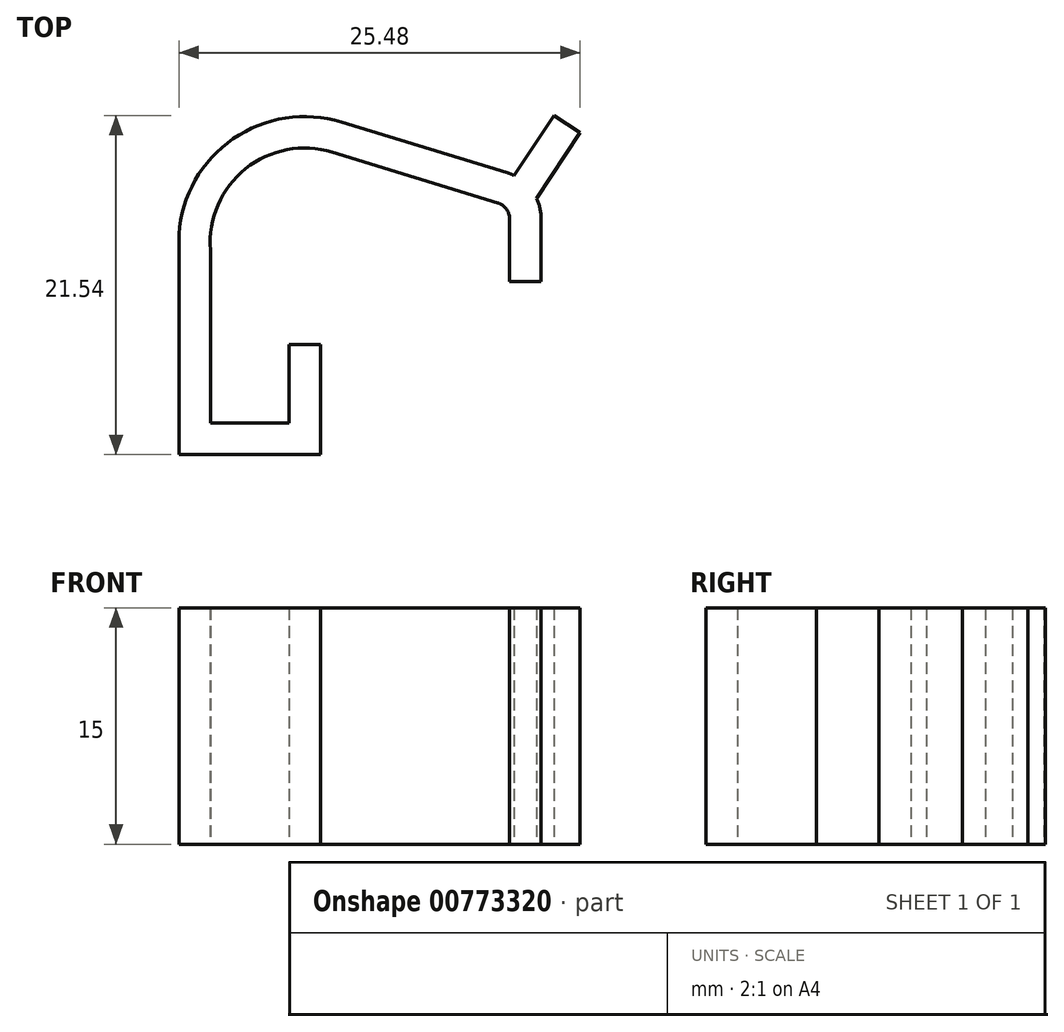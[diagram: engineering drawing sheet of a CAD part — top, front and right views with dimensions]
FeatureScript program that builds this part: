
annotation { "Feature Type Name" : "Feature", "Feature Type Description" : "" }
export const myFeature = defineFeature(function(context is Context, id is Id, definition is map)
    precondition{}
    {
        {
            var Q0;
            Q0=qCreatedBy(makeId("Top.planeOp"),FACE);
            var sketch = newSketch(context, id + "F0", { "sketchPlane" : qUnion([Q0])});
            skLineSegment(sketch, "E0", {"start": v(2, 32) * mm, "end": v(7, 32) * mm});
            skLineSegment(sketch, "E1", {"start": v(7, 32) * mm, "end": v(7, 37) * mm});
            skLineSegment(sketch, "E2", {"start": v(7, 37) * mm, "end": v(9, 37) * mm});
            skLineSegment(sketch, "E3", {"start": v(9, 37) * mm, "end": v(9, 30) * mm});
            skLineSegment(sketch, "E4", {"start": v(9, 30) * mm, "end": v(0, 30) * mm});
            skLineSegment(sketch, "E5", {"start": v(0, 30) * mm, "end": v(0, 44) * mm});
            skLineSegment(sketch, "E6", {"start": v(2, 32) * mm, "end": v(2, 43) * mm});
            skArc(sketch, "E7", {"start": v(9.74, 49.2) * mm, "mid": v(4.23, 48.15) * mm, "end": v(2, 43) * mm});
            skArc(sketch, "E8", {"start": v(10.32, 51.11) * mm, "mid": v(3.44, 50.05) * mm, "end": v(0, 44) * mm});
            skLineSegment(sketch, "E9", {"start": v(9.74, 49.2) * mm, "end": v(20.26, 45.98) * mm});
            skArc(sketch, "E10", {"start": v(20.26, 45.98) * mm, "mid": v(20.8, 45.6) * mm, "end": v(21, 44.98) * mm});
            skLineSegment(sketch, "E11", {"start": v(21, 44.98) * mm, "end": v(21, 40.98) * mm});
            skLineSegment(sketch, "E12", {"start": v(21, 40.98) * mm, "end": v(23, 40.98) * mm});
            skLineSegment(sketch, "E13", {"start": v(23, 44.98) * mm, "end": v(23, 40.98) * mm});
            skLineSegment(sketch, "E14", {"start": v(21.28, 47.72) * mm, "end": v(23.81, 51.54) * mm});
            skLineSegment(sketch, "E15", {"start": v(23.81, 51.54) * mm, "end": v(25.48, 50.43) * mm});
            skLineSegment(sketch, "E16", {"start": v(25.48, 50.43) * mm, "end": v(22.71, 46.27) * mm});
            skLineSegment(sketch, "E17", {"start": v(10.32, 51.11) * mm, "end": v(20.84, 47.9) * mm});
            skLineSegment(sketch, "E18", {"start": v(10.32, 51.11) * mm, "end": v(9.74, 49.2) * mm});
            skLineSegment(sketch, "E19", {"start": v(20.84, 47.9) * mm, "end": v(20.26, 45.98) * mm});
            skLineSegment(sketch, "E20", {"start": v(21, 44.98) * mm, "end": v(23, 44.98) * mm});
            skArc(sketch, "E21", {"start": v(20.84, 47.9) * mm, "mid": v(22.4, 46.8) * mm, "end": v(23, 44.98) * mm});
            skSolve(sketch);
        }
        {
            var Q0;
            Q0 = qSketchRegion(id + "F0", true);
            var Q1;
            Q1 = qSketchRegion(id + "F2", true);
            extrude(context, id + "F1", {"entities" : qUnion([Q0, Q1]), "depth" : 15 * mm, "offsetDistance" : 25 * mm});
        }
        {
            var Q0;
            Q0=qCreatedBy(makeId("Top.planeOp"),FACE);
            var sketch = newSketch(context, id + "F2", { "sketchPlane" : qUnion([Q0])});
            skLineSegment(sketch, "E22.0.1.0", {"start": v(-38.8, -34.92) * mm, "end": v(-38.8, -38.92) * mm});
            skLineSegment(sketch, "E22.0.1.1", {"start": v(-50.06, -30.7) * mm, "end": v(-39.54, -33.92) * mm});
            skArc(sketch, "E22.0.1.2", {"start": v(-49.48, -28.79) * mm, "mid": v(-56.36, -29.85) * mm, "end": v(-59.8, -35.9) * mm});
            skArc(sketch, "E22.0.1.3", {"start": v(-50.06, -30.7) * mm, "mid": v(-55.57, -31.75) * mm, "end": v(-57.8, -36.9) * mm});
            skLineSegment(sketch, "E22.0.1.4", {"start": v(-57.8, -47.9) * mm, "end": v(-57.8, -36.9) * mm});
            skLineSegment(sketch, "E22.0.1.5", {"start": v(-59.8, -49.9) * mm, "end": v(-59.8, -35.9) * mm});
            skLineSegment(sketch, "E22.0.1.6", {"start": v(-50.8, -49.9) * mm, "end": v(-59.8, -49.9) * mm});
            skLineSegment(sketch, "E22.0.1.7", {"start": v(-50.8, -42.9) * mm, "end": v(-50.8, -49.9) * mm});
            skLineSegment(sketch, "E22.0.1.8", {"start": v(-52.8, -47.9) * mm, "end": v(-52.8, -42.9) * mm});
            skLineSegment(sketch, "E22.0.1.9", {"start": v(-57.8, -47.9) * mm, "end": v(-52.8, -47.9) * mm});
            skLineSegment(sketch, "E22.0.1.10", {"start": v(-38.52, -32.18) * mm, "end": v(-35.99, -28.36) * mm});
            skLineSegment(sketch, "E22.0.1.11", {"start": v(-49.48, -28.79) * mm, "end": v(-38.96, -32) * mm});
            skLineSegment(sketch, "E22.0.1.12", {"start": v(-34.32, -29.47) * mm, "end": v(-37.09, -33.63) * mm});
            skLineSegment(sketch, "E22.0.1.13", {"start": v(-36.8, -34.92) * mm, "end": v(-36.8, -38.92) * mm});
            skArc(sketch, "E22.0.1.14", {"start": v(-38.96, -32) * mm, "mid": v(-37.4, -33.1) * mm, "end": v(-36.8, -34.92) * mm});
            skLineSegment(sketch, "E22.0.1.15", {"start": v(-38.8, -38.92) * mm, "end": v(-36.8, -38.92) * mm});
            skLineSegment(sketch, "E22.0.1.16", {"start": v(-52.8, -42.9) * mm, "end": v(-50.8, -42.9) * mm});
            skLineSegment(sketch, "E22.0.1.17", {"start": v(-35.99, -28.36) * mm, "end": v(-34.32, -29.47) * mm});
            skLineSegment(sketch, "E22.0.1.18", {"start": v(-38.96, -32) * mm, "end": v(-39.54, -33.92) * mm});
            skLineSegment(sketch, "E22.0.1.19", {"start": v(-49.48, -28.79) * mm, "end": v(-50.06, -30.7) * mm});
            skArc(sketch, "E22.0.1.20", {"start": v(-39.54, -33.92) * mm, "mid": v(-39, -34.3) * mm, "end": v(-38.8, -34.92) * mm});
            skLineSegment(sketch, "E22.0.1.21", {"start": v(-38.8, -34.92) * mm, "end": v(-36.8, -34.92) * mm});
            skLineSegment(sketch, "E22.1.0.0", {"start": v(32.03, 2) * mm, "end": v(32.03, -2) * mm});
            skLineSegment(sketch, "E22.1.0.1", {"start": v(20.77, 6.23) * mm, "end": v(31.3, 3) * mm});
            skArc(sketch, "E22.1.0.2", {"start": v(21.36, 8.14) * mm, "mid": v(14.48, 7.08) * mm, "end": v(11.03, 1.03) * mm});
            skArc(sketch, "E22.1.0.3", {"start": v(20.77, 6.23) * mm, "mid": v(15.26, 5.17) * mm, "end": v(13.03, 0.03) * mm});
            skLineSegment(sketch, "E22.1.0.4", {"start": v(13.03, -10.97) * mm, "end": v(13.03, 0.03) * mm});
            skLineSegment(sketch, "E22.1.0.5", {"start": v(11.03, -12.97) * mm, "end": v(11.03, 1.03) * mm});
            skLineSegment(sketch, "E22.1.0.6", {"start": v(20.03, -12.97) * mm, "end": v(11.03, -12.97) * mm});
            skLineSegment(sketch, "E22.1.0.7", {"start": v(20.03, -5.97) * mm, "end": v(20.03, -12.97) * mm});
            skLineSegment(sketch, "E22.1.0.8", {"start": v(18.03, -10.97) * mm, "end": v(18.03, -5.97) * mm});
            skLineSegment(sketch, "E22.1.0.9", {"start": v(13.03, -10.97) * mm, "end": v(18.03, -10.97) * mm});
            skLineSegment(sketch, "E22.1.0.10", {"start": v(32.31, 4.75) * mm, "end": v(34.85, 8.57) * mm});
            skLineSegment(sketch, "E22.1.0.11", {"start": v(21.36, 8.14) * mm, "end": v(31.88, 4.92) * mm});
            skLineSegment(sketch, "E22.1.0.12", {"start": v(36.51, 7.46) * mm, "end": v(33.75, 3.3) * mm});
            skLineSegment(sketch, "E22.1.0.13", {"start": v(34.03, 2) * mm, "end": v(34.03, -2) * mm});
            skArc(sketch, "E22.1.0.14", {"start": v(31.88, 4.92) * mm, "mid": v(33.44, 3.82) * mm, "end": v(34.03, 2) * mm});
            skLineSegment(sketch, "E22.1.0.15", {"start": v(32.03, -2) * mm, "end": v(34.03, -2) * mm});
            skLineSegment(sketch, "E22.1.0.16", {"start": v(18.03, -5.97) * mm, "end": v(20.03, -5.97) * mm});
            skLineSegment(sketch, "E22.1.0.17", {"start": v(34.85, 8.57) * mm, "end": v(36.51, 7.46) * mm});
            skLineSegment(sketch, "E22.1.0.18", {"start": v(31.88, 4.92) * mm, "end": v(31.3, 3) * mm});
            skLineSegment(sketch, "E22.1.0.19", {"start": v(21.36, 8.14) * mm, "end": v(20.77, 6.23) * mm});
            skArc(sketch, "E22.1.0.20", {"start": v(31.3, 3) * mm, "mid": v(31.83, 2.63) * mm, "end": v(32.03, 2) * mm});
            skLineSegment(sketch, "E22.1.0.21", {"start": v(32.03, 2) * mm, "end": v(34.03, 2) * mm});
            skLineSegment(sketch, "E22.1.1.0", {"start": v(-13.8, -34.92) * mm, "end": v(-13.8, -38.92) * mm});
            skLineSegment(sketch, "E22.1.1.1", {"start": v(-25.06, -30.7) * mm, "end": v(-14.54, -33.92) * mm});
            skArc(sketch, "E22.1.1.2", {"start": v(-24.48, -28.79) * mm, "mid": v(-31.36, -29.85) * mm, "end": v(-34.8, -35.9) * mm});
            skArc(sketch, "E22.1.1.3", {"start": v(-25.06, -30.7) * mm, "mid": v(-30.57, -31.75) * mm, "end": v(-32.8, -36.9) * mm});
            skLineSegment(sketch, "E22.1.1.4", {"start": v(-32.8, -47.9) * mm, "end": v(-32.8, -36.9) * mm});
            skLineSegment(sketch, "E22.1.1.5", {"start": v(-34.8, -49.9) * mm, "end": v(-34.8, -35.9) * mm});
            skLineSegment(sketch, "E22.1.1.6", {"start": v(-25.8, -49.9) * mm, "end": v(-34.8, -49.9) * mm});
            skLineSegment(sketch, "E22.1.1.7", {"start": v(-25.8, -42.9) * mm, "end": v(-25.8, -49.9) * mm});
            skLineSegment(sketch, "E22.1.1.8", {"start": v(-27.8, -47.9) * mm, "end": v(-27.8, -42.9) * mm});
            skLineSegment(sketch, "E22.1.1.9", {"start": v(-32.8, -47.9) * mm, "end": v(-27.8, -47.9) * mm});
            skLineSegment(sketch, "E22.1.1.10", {"start": v(-13.52, -32.18) * mm, "end": v(-10.99, -28.36) * mm});
            skLineSegment(sketch, "E22.1.1.11", {"start": v(-24.48, -28.79) * mm, "end": v(-13.96, -32) * mm});
            skLineSegment(sketch, "E22.1.1.12", {"start": v(-9.32, -29.47) * mm, "end": v(-12.09, -33.63) * mm});
            skLineSegment(sketch, "E22.1.1.13", {"start": v(-11.8, -34.92) * mm, "end": v(-11.8, -38.92) * mm});
            skArc(sketch, "E22.1.1.14", {"start": v(-13.96, -32) * mm, "mid": v(-12.4, -33.1) * mm, "end": v(-11.8, -34.92) * mm});
            skLineSegment(sketch, "E22.1.1.15", {"start": v(-13.8, -38.92) * mm, "end": v(-11.8, -38.92) * mm});
            skLineSegment(sketch, "E22.1.1.16", {"start": v(-27.8, -42.9) * mm, "end": v(-25.8, -42.9) * mm});
            skLineSegment(sketch, "E22.1.1.17", {"start": v(-10.99, -28.36) * mm, "end": v(-9.32, -29.47) * mm});
            skLineSegment(sketch, "E22.1.1.18", {"start": v(-13.96, -32) * mm, "end": v(-14.54, -33.92) * mm});
            skLineSegment(sketch, "E22.1.1.19", {"start": v(-24.48, -28.79) * mm, "end": v(-25.06, -30.7) * mm});
            skArc(sketch, "E22.1.1.20", {"start": v(-14.54, -33.92) * mm, "mid": v(-14, -34.3) * mm, "end": v(-13.8, -34.92) * mm});
            skLineSegment(sketch, "E22.1.1.21", {"start": v(-13.8, -34.92) * mm, "end": v(-11.8, -34.92) * mm});
            skLineSegment(sketch, "E22.2.0.0", {"start": v(57.03, 2) * mm, "end": v(57.03, -2) * mm});
            skLineSegment(sketch, "E22.2.0.1", {"start": v(45.77, 6.23) * mm, "end": v(56.3, 3) * mm});
            skArc(sketch, "E22.2.0.2", {"start": v(46.36, 8.14) * mm, "mid": v(39.48, 7.08) * mm, "end": v(36.03, 1.03) * mm});
            skArc(sketch, "E22.2.0.3", {"start": v(45.77, 6.23) * mm, "mid": v(40.26, 5.17) * mm, "end": v(38.03, 0.03) * mm});
            skLineSegment(sketch, "E22.2.0.4", {"start": v(38.03, -10.97) * mm, "end": v(38.03, 0.03) * mm});
            skLineSegment(sketch, "E22.2.0.5", {"start": v(36.03, -12.97) * mm, "end": v(36.03, 1.03) * mm});
            skLineSegment(sketch, "E22.2.0.6", {"start": v(45.03, -12.97) * mm, "end": v(36.03, -12.97) * mm});
            skLineSegment(sketch, "E22.2.0.7", {"start": v(45.03, -5.97) * mm, "end": v(45.03, -12.97) * mm});
            skLineSegment(sketch, "E22.2.0.8", {"start": v(43.03, -10.97) * mm, "end": v(43.03, -5.97) * mm});
            skLineSegment(sketch, "E22.2.0.9", {"start": v(38.03, -10.97) * mm, "end": v(43.03, -10.97) * mm});
            skLineSegment(sketch, "E22.2.0.10", {"start": v(57.31, 4.75) * mm, "end": v(59.85, 8.57) * mm});
            skLineSegment(sketch, "E22.2.0.11", {"start": v(46.36, 8.14) * mm, "end": v(56.88, 4.92) * mm});
            skLineSegment(sketch, "E22.2.0.12", {"start": v(61.51, 7.46) * mm, "end": v(58.75, 3.3) * mm});
            skLineSegment(sketch, "E22.2.0.13", {"start": v(59.03, 2) * mm, "end": v(59.03, -2) * mm});
            skArc(sketch, "E22.2.0.14", {"start": v(56.88, 4.92) * mm, "mid": v(58.44, 3.82) * mm, "end": v(59.03, 2) * mm});
            skLineSegment(sketch, "E22.2.0.15", {"start": v(57.03, -2) * mm, "end": v(59.03, -2) * mm});
            skLineSegment(sketch, "E22.2.0.16", {"start": v(43.03, -5.97) * mm, "end": v(45.03, -5.97) * mm});
            skLineSegment(sketch, "E22.2.0.17", {"start": v(59.85, 8.57) * mm, "end": v(61.51, 7.46) * mm});
            skLineSegment(sketch, "E22.2.0.18", {"start": v(56.88, 4.92) * mm, "end": v(56.3, 3) * mm});
            skLineSegment(sketch, "E22.2.0.19", {"start": v(46.36, 8.14) * mm, "end": v(45.77, 6.23) * mm});
            skArc(sketch, "E22.2.0.20", {"start": v(56.3, 3) * mm, "mid": v(56.83, 2.63) * mm, "end": v(57.03, 2) * mm});
            skLineSegment(sketch, "E22.2.0.21", {"start": v(57.03, 2) * mm, "end": v(59.03, 2) * mm});
            skLineSegment(sketch, "E22.2.1.0", {"start": v(11.2, -34.92) * mm, "end": v(11.2, -38.92) * mm});
            skLineSegment(sketch, "E22.2.1.1", {"start": v(-0.06, -30.7) * mm, "end": v(10.46, -33.92) * mm});
            skArc(sketch, "E22.2.1.2", {"start": v(0.52, -28.79) * mm, "mid": v(-6.36, -29.85) * mm, "end": v(-9.8, -35.9) * mm});
            skArc(sketch, "E22.2.1.3", {"start": v(-0.06, -30.7) * mm, "mid": v(-5.57, -31.75) * mm, "end": v(-7.8, -36.9) * mm});
            skLineSegment(sketch, "E22.2.1.4", {"start": v(-7.8, -47.9) * mm, "end": v(-7.8, -36.9) * mm});
            skLineSegment(sketch, "E22.2.1.5", {"start": v(-9.8, -49.9) * mm, "end": v(-9.8, -35.9) * mm});
            skLineSegment(sketch, "E22.2.1.6", {"start": v(-0.8, -49.9) * mm, "end": v(-9.8, -49.9) * mm});
            skLineSegment(sketch, "E22.2.1.7", {"start": v(-0.8, -42.9) * mm, "end": v(-0.8, -49.9) * mm});
            skLineSegment(sketch, "E22.2.1.8", {"start": v(-2.8, -47.9) * mm, "end": v(-2.8, -42.9) * mm});
            skLineSegment(sketch, "E22.2.1.9", {"start": v(-7.8, -47.9) * mm, "end": v(-2.8, -47.9) * mm});
            skLineSegment(sketch, "E22.2.1.10", {"start": v(11.48, -32.18) * mm, "end": v(14.01, -28.36) * mm});
            skLineSegment(sketch, "E22.2.1.11", {"start": v(0.52, -28.79) * mm, "end": v(11.04, -32) * mm});
            skLineSegment(sketch, "E22.2.1.12", {"start": v(15.68, -29.47) * mm, "end": v(12.91, -33.63) * mm});
            skLineSegment(sketch, "E22.2.1.13", {"start": v(13.2, -34.92) * mm, "end": v(13.2, -38.92) * mm});
            skArc(sketch, "E22.2.1.14", {"start": v(11.04, -32) * mm, "mid": v(12.6, -33.1) * mm, "end": v(13.2, -34.92) * mm});
            skLineSegment(sketch, "E22.2.1.15", {"start": v(11.2, -38.92) * mm, "end": v(13.2, -38.92) * mm});
            skLineSegment(sketch, "E22.2.1.16", {"start": v(-2.8, -42.9) * mm, "end": v(-0.8, -42.9) * mm});
            skLineSegment(sketch, "E22.2.1.17", {"start": v(14.01, -28.36) * mm, "end": v(15.68, -29.47) * mm});
            skLineSegment(sketch, "E22.2.1.18", {"start": v(11.04, -32) * mm, "end": v(10.46, -33.92) * mm});
            skLineSegment(sketch, "E22.2.1.19", {"start": v(0.52, -28.79) * mm, "end": v(-0.06, -30.7) * mm});
            skArc(sketch, "E22.2.1.20", {"start": v(10.46, -33.92) * mm, "mid": v(11, -34.3) * mm, "end": v(11.2, -34.92) * mm});
            skLineSegment(sketch, "E22.2.1.21", {"start": v(11.2, -34.92) * mm, "end": v(13.2, -34.92) * mm});
            skLineSegment(sketch, "E22.direction1", {"start": v(-13.97, -12.97) * mm, "end": v(11.03, -12.97) * mm, "construction": true});
            skLineSegment(sketch, "E22.direction2", {"start": v(-13.97, -12.97) * mm, "end": v(-59.8, -49.9) * mm, "construction": true});
            skSolve(sketch);
        }
        {
            var Q0;
            Q0 = qSketchRegion(id + "F2", true);
            extrude(context, id + "F3", {"entities" : qUnion([Q0]), "depth" : 15 * mm, "offsetDistance" : 25 * mm});
        }
        {
            var Q0;
            Q0=makeQuery(id+"F3.opExtrude","SWEPT_BODY",BODY,{"disambiguationData":[OSD([sQuery(id+"F2.wireOp",EDGE,"E22.1.0.0"),sQuery(id+"F2.wireOp",EDGE,"E22.1.0.1"),sQuery(id+"F2.wireOp",EDGE,"E22.1.0.2"),sQuery(id+"F2.wireOp",EDGE,"E22.1.0.3"),sQuery(id+"F2.wireOp",EDGE,"E22.1.0.4"),sQuery(id+"F2.wireOp",EDGE,"E22.1.0.5"),sQuery(id+"F2.wireOp",EDGE,"E22.1.0.6"),sQuery(id+"F2.wireOp",EDGE,"E22.1.0.7"),sQuery(id+"F2.wireOp",EDGE,"E22.1.0.8"),sQuery(id+"F2.wireOp",EDGE,"E22.1.0.9"),sQuery(id+"F2.wireOp",EDGE,"E22.1.0.10"),sQuery(id+"F2.wireOp",EDGE,"E22.1.0.11"),sQuery(id+"F2.wireOp",EDGE,"E22.1.0.12"),sQuery(id+"F2.wireOp",EDGE,"E22.1.0.13"),sQuery(id+"F2.wireOp",EDGE,"E22.1.0.14"),sQuery(id+"F2.wireOp",EDGE,"E22.1.0.15"),sQuery(id+"F2.wireOp",EDGE,"E22.1.0.16"),sQuery(id+"F2.wireOp",EDGE,"E22.1.0.17"),sQuery(id+"F2.wireOp",EDGE,"E22.1.0.20")])]});
            var Q1;
            Q1=makeQuery(id+"F3.opExtrude","SWEPT_BODY",BODY,{"disambiguationData":[OSD([sQuery(id+"F2.wireOp",EDGE,"E22.0.1.0"),sQuery(id+"F2.wireOp",EDGE,"E22.0.1.1"),sQuery(id+"F2.wireOp",EDGE,"E22.0.1.2"),sQuery(id+"F2.wireOp",EDGE,"E22.0.1.3"),sQuery(id+"F2.wireOp",EDGE,"E22.0.1.4"),sQuery(id+"F2.wireOp",EDGE,"E22.0.1.5"),sQuery(id+"F2.wireOp",EDGE,"E22.0.1.6"),sQuery(id+"F2.wireOp",EDGE,"E22.0.1.7"),sQuery(id+"F2.wireOp",EDGE,"E22.0.1.8"),sQuery(id+"F2.wireOp",EDGE,"E22.0.1.9"),sQuery(id+"F2.wireOp",EDGE,"E22.0.1.10"),sQuery(id+"F2.wireOp",EDGE,"E22.0.1.11"),sQuery(id+"F2.wireOp",EDGE,"E22.0.1.12"),sQuery(id+"F2.wireOp",EDGE,"E22.0.1.13"),sQuery(id+"F2.wireOp",EDGE,"E22.0.1.14"),sQuery(id+"F2.wireOp",EDGE,"E22.0.1.15"),sQuery(id+"F2.wireOp",EDGE,"E22.0.1.16"),sQuery(id+"F2.wireOp",EDGE,"E22.0.1.17"),sQuery(id+"F2.wireOp",EDGE,"E22.0.1.20")])]});
            var Q2;
            Q2=makeQuery(id+"F3.opExtrude","SWEPT_BODY",BODY,{"disambiguationData":[OSD([sQuery(id+"F2.wireOp",EDGE,"E22.1.1.0"),sQuery(id+"F2.wireOp",EDGE,"E22.1.1.1"),sQuery(id+"F2.wireOp",EDGE,"E22.1.1.2"),sQuery(id+"F2.wireOp",EDGE,"E22.1.1.3"),sQuery(id+"F2.wireOp",EDGE,"E22.1.1.4"),sQuery(id+"F2.wireOp",EDGE,"E22.1.1.5"),sQuery(id+"F2.wireOp",EDGE,"E22.1.1.6"),sQuery(id+"F2.wireOp",EDGE,"E22.1.1.7"),sQuery(id+"F2.wireOp",EDGE,"E22.1.1.8"),sQuery(id+"F2.wireOp",EDGE,"E22.1.1.9"),sQuery(id+"F2.wireOp",EDGE,"E22.1.1.10"),sQuery(id+"F2.wireOp",EDGE,"E22.1.1.11"),sQuery(id+"F2.wireOp",EDGE,"E22.1.1.12"),sQuery(id+"F2.wireOp",EDGE,"E22.1.1.13"),sQuery(id+"F2.wireOp",EDGE,"E22.1.1.14"),sQuery(id+"F2.wireOp",EDGE,"E22.1.1.15"),sQuery(id+"F2.wireOp",EDGE,"E22.1.1.16"),sQuery(id+"F2.wireOp",EDGE,"E22.1.1.17"),sQuery(id+"F2.wireOp",EDGE,"E22.1.1.20")])]});
            var Q3;
            Q3=makeQuery(id+"F3.opExtrude","SWEPT_BODY",BODY,{"disambiguationData":[OSD([sQuery(id+"F2.wireOp",EDGE,"E22.2.0.0"),sQuery(id+"F2.wireOp",EDGE,"E22.2.0.1"),sQuery(id+"F2.wireOp",EDGE,"E22.2.0.2"),sQuery(id+"F2.wireOp",EDGE,"E22.2.0.3"),sQuery(id+"F2.wireOp",EDGE,"E22.2.0.4"),sQuery(id+"F2.wireOp",EDGE,"E22.2.0.5"),sQuery(id+"F2.wireOp",EDGE,"E22.2.0.6"),sQuery(id+"F2.wireOp",EDGE,"E22.2.0.7"),sQuery(id+"F2.wireOp",EDGE,"E22.2.0.8"),sQuery(id+"F2.wireOp",EDGE,"E22.2.0.9"),sQuery(id+"F2.wireOp",EDGE,"E22.2.0.10"),sQuery(id+"F2.wireOp",EDGE,"E22.2.0.11"),sQuery(id+"F2.wireOp",EDGE,"E22.2.0.12"),sQuery(id+"F2.wireOp",EDGE,"E22.2.0.13"),sQuery(id+"F2.wireOp",EDGE,"E22.2.0.14"),sQuery(id+"F2.wireOp",EDGE,"E22.2.0.15"),sQuery(id+"F2.wireOp",EDGE,"E22.2.0.16"),sQuery(id+"F2.wireOp",EDGE,"E22.2.0.17"),sQuery(id+"F2.wireOp",EDGE,"E22.2.0.20")])]});
            var Q4;
            Q4=makeQuery(id+"F3.opExtrude","SWEPT_BODY",BODY,{"disambiguationData":[OSD([sQuery(id+"F2.wireOp",EDGE,"E22.2.1.0"),sQuery(id+"F2.wireOp",EDGE,"E22.2.1.1"),sQuery(id+"F2.wireOp",EDGE,"E22.2.1.2"),sQuery(id+"F2.wireOp",EDGE,"E22.2.1.3"),sQuery(id+"F2.wireOp",EDGE,"E22.2.1.4"),sQuery(id+"F2.wireOp",EDGE,"E22.2.1.5"),sQuery(id+"F2.wireOp",EDGE,"E22.2.1.6"),sQuery(id+"F2.wireOp",EDGE,"E22.2.1.7"),sQuery(id+"F2.wireOp",EDGE,"E22.2.1.8"),sQuery(id+"F2.wireOp",EDGE,"E22.2.1.9"),sQuery(id+"F2.wireOp",EDGE,"E22.2.1.10"),sQuery(id+"F2.wireOp",EDGE,"E22.2.1.11"),sQuery(id+"F2.wireOp",EDGE,"E22.2.1.12"),sQuery(id+"F2.wireOp",EDGE,"E22.2.1.13"),sQuery(id+"F2.wireOp",EDGE,"E22.2.1.14"),sQuery(id+"F2.wireOp",EDGE,"E22.2.1.15"),sQuery(id+"F2.wireOp",EDGE,"E22.2.1.16"),sQuery(id+"F2.wireOp",EDGE,"E22.2.1.17"),sQuery(id+"F2.wireOp",EDGE,"E22.2.1.20")])]});
            deleteBodies(context, id + "F4", {"entities" : qUnion([Q0, Q1, Q2, Q3, Q4])});
        }
        {
            var Q0;
            Q0=makeQuery(id+"F1.opExtrude","SWEPT_BODY",BODY,{"disambiguationData":[OSD([sQuery(id+"F0.wireOp",EDGE,"E0"),sQuery(id+"F0.wireOp",EDGE,"E1"),sQuery(id+"F0.wireOp",EDGE,"E2"),sQuery(id+"F0.wireOp",EDGE,"E3"),sQuery(id+"F0.wireOp",EDGE,"E4"),sQuery(id+"F0.wireOp",EDGE,"E5"),sQuery(id+"F0.wireOp",EDGE,"E6"),sQuery(id+"F0.wireOp",EDGE,"E7"),sQuery(id+"F0.wireOp",EDGE,"E8"),sQuery(id+"F0.wireOp",EDGE,"E9"),sQuery(id+"F0.wireOp",EDGE,"E10"),sQuery(id+"F0.wireOp",EDGE,"E11"),sQuery(id+"F0.wireOp",EDGE,"E12"),sQuery(id+"F0.wireOp",EDGE,"E13"),sQuery(id+"F0.wireOp",EDGE,"E14"),sQuery(id+"F0.wireOp",EDGE,"E15"),sQuery(id+"F0.wireOp",EDGE,"E16"),sQuery(id+"F0.wireOp",EDGE,"E17"),sQuery(id+"F0.wireOp",EDGE,"E21")])]});
            transform(context, id + "F5", {"entities" : qUnion([Q0]), "transformType" : TransformType.TRANSLATION_3D, "dx" : -10.3 * mm, "dy" : -40.1 * mm, "dz" : 0 * mm, "makeCopy" : false});
        }
    });
